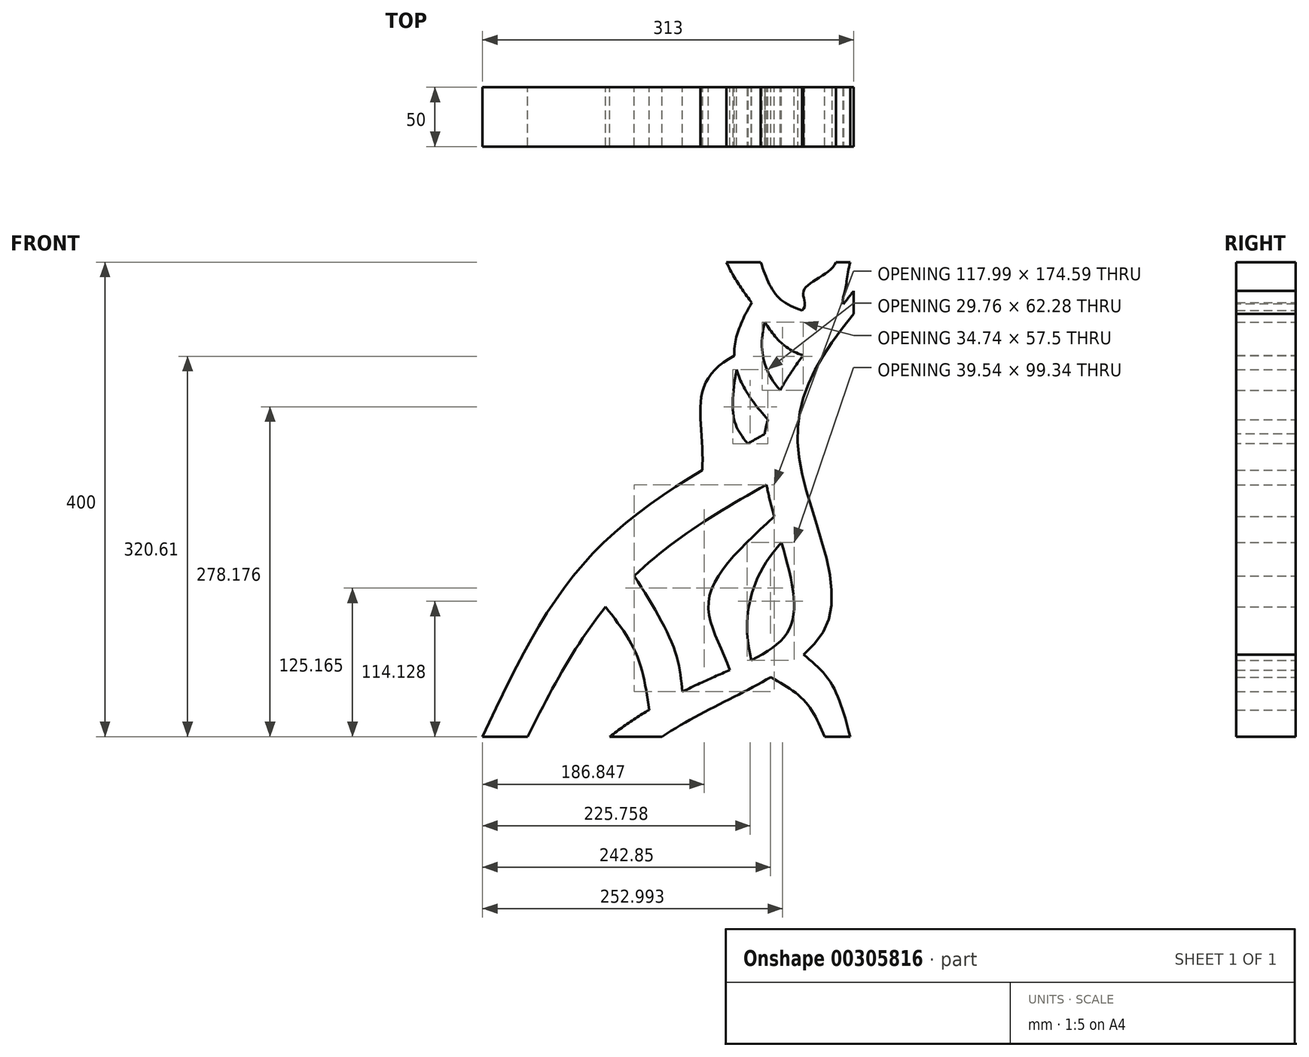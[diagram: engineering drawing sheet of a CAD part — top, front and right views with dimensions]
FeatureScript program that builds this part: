
annotation { "Feature Type Name" : "Feature", "Feature Type Description" : "" }
export const myFeature = defineFeature(function(context is Context, id is Id, definition is map)
    precondition{}
    {
        {
            var Q0;
            Q0=qCreatedBy(makeId("Front.planeOp"),FACE);
            var sketch = newSketch(context, id + "F0", { "sketchPlane" : qUnion([Q0])});
            skLineSegment(sketch, "E0.bottom", {"start": v(161.57, 207.7) * mm, "end": v(-151.43, 207.7) * mm});
            skLineSegment(sketch, "E0.top", {"start": v(161.57, -192.3) * mm, "end": v(-151.43, -192.3) * mm});
            skLineSegment(sketch, "E0.left", {"start": v(161.57, 207.7) * mm, "end": v(161.57, -192.3) * mm});
            skLineSegment(sketch, "E0.right", {"start": v(-151.43, 207.7) * mm, "end": v(-151.43, -192.3) * mm});
            skFitSpline(sketch, "E1", {"points": [v(161.57, 183.5) * mm, v(85.12, 44.75) * mm, v(109.31, -96.4) * mm, v(-44.12, -192.3) * mm], "startDerivative": vector(-382, -492.17) * mm, "endDerivative": vector(-632.26, -490) * mm});
            skFitSpline(sketch, "E2", {"points": [v(161.57, 164.23) * mm, v(115.12, 45.06) * mm, v(139.33, -96.46) * mm, v(0, -192.3) * mm], "startDerivative": vector(-323.93, -389.82) * mm, "endDerivative": vector(-432.8, -289.86) * mm});
            skFitSpline(sketch, "E3", {"points": [v(87.95, 20.15) * mm, v(-36.08, -69.46) * mm, v(-113.36, -192.3) * mm], "startDerivative": vector(-287.2, -159.14) * mm, "endDerivative": vector(-134.26, -271.05) * mm});
            skFitSpline(sketch, "E4", {"points": [v(86.4, 62.77) * mm, v(-60.96, -40.6) * mm, v(-151.43, -192.3) * mm], "startDerivative": vector(-322.1, -181.09) * mm, "endDerivative": vector(-154.33, -329.73) * mm});
            skFitSpline(sketch, "E5", {"points": [v(91.66, -142.16) * mm, v(120.33, -162.57) * mm, v(137.1, -192.3) * mm], "startDerivative": vector(63.12, -36.39) * mm, "endDerivative": vector(28.09, -64.9) * mm});
            skFitSpline(sketch, "E6", {"points": [v(119.32, -123.08) * mm, v(142.68, -147.67) * mm, v(158.5, -192.3) * mm], "startDerivative": vector(55.7, -46.78) * mm, "endDerivative": vector(23.32, -90.23) * mm});
            skFitSpline(sketch, "E7", {"points": [v(100.65, -28.51) * mm, v(73.78, -78.77) * mm, v(75.03, -127.85) * mm], "startDerivative": vector(-88.91, -98.41) * mm, "endDerivative": vector(24.95, -113.83) * mm});
            skFitSpline(sketch, "E8", {"points": [v(94.41, -6.72) * mm, v(39.45, -75.98) * mm, v(57.07, -136.12) * mm], "startDerivative": vector(-135.48, -128.88) * mm, "endDerivative": vector(50.2, -141.27) * mm});
            skFitSpline(sketch, "E9", {"points": [v(54.23, 207.7) * mm, v(81.23, 165.16) * mm, v(119.4, 129.17) * mm], "startDerivative": vector(44.56, -99.42) * mm, "endDerivative": vector(118.17, -31.75) * mm});
            skFitSpline(sketch, "E10", {"points": [v(83.1, 207.7) * mm, v(99.85, 176.33) * mm, v(142.84, 159.86) * mm], "startDerivative": vector(25.78, -76.02) * mm, "endDerivative": vector(99.84, -29.98) * mm});
            skFitSpline(sketch, "E11", {"points": [v(146.4, 207.7) * mm, v(119.4, 183.78) * mm, v(118, 167.02) * mm], "startDerivative": vector(-16.59, -50.41) * mm, "endDerivative": vector(-40.58, -34) * mm});
            skFitSpline(sketch, "E12", {"points": [v(158.5, 207.7) * mm, v(153.85, 181.92) * mm, v(152.97, 172.55) * mm], "startDerivative": vector(-12.64, -48.27) * mm, "endDerivative": vector(10.98, -30.7) * mm});
            skFitSpline(sketch, "E13", {"points": [v(75.43, 173.52) * mm, v(60.75, 128.85) * mm, v(89.2, 75) * mm], "startDerivative": vector(-54.24, -96.72) * mm, "endDerivative": vector(96.14, -103.87) * mm});
            skFitSpline(sketch, "E14", {"points": [v(86.56, 157.05) * mm, v(84.95, 128.85) * mm, v(99.53, 99.55) * mm], "startDerivative": vector(-16.02, -62.32) * mm, "endDerivative": vector(51.54, -60.1) * mm});
            skFitSpline(sketch, "E15", {"points": [v(62.75, 117) * mm, v(60.75, 74.85) * mm, v(72.13, 54.73) * mm], "startDerivative": vector(-16.42, -83.23) * mm, "endDerivative": vector(39.32, -49.75) * mm});
            skFitSpline(sketch, "E16", {"points": [v(60.75, 128.85) * mm, v(35.6, 103.71) * mm, v(32.47, 71.12) * mm, v(33.78, 32.44) * mm], "startDerivative": vector(-112.87, -59.98) * mm, "endDerivative": vector(-6.89, -98.92) * mm});
            skFitSpline(sketch, "E17", {"points": [v(-47.68, -82.88) * mm, v(-21.54, -123.28) * mm, v(-11.06, -169.71) * mm], "startDerivative": vector(59.74, -77.34) * mm, "endDerivative": vector(13.37, -96.33) * mm});
            skFitSpline(sketch, "E18", {"points": [v(-23.58, -56.72) * mm, v(10.06, -118.02) * mm, v(16.93, -154.44) * mm], "startDerivative": vector(70.14, -111.5) * mm, "endDerivative": vector(7.52, -82.35) * mm});
            skSolve(sketch);
        }
        {
            var Q0;
            {var subQ0=sQuery(id+"F0.wireOp",EDGE,"E3");var subQ3=sQuery(id+"F0.wireOp",EDGE,"E1");var subQ4=makeQuery(id+"F0.imprint","INTERSECT",VERTEX,{"derivedFrom":[subQ3,subQ0]});Q0=makeQuery(id+"F0.imprint","IMPRINT",FACE,{"disambiguationData":[TD([[makeQuery(id+"F0.imprint","IMPRINT",EDGE,{"disambiguationData":[TD([[subQ4,1.0]])],"derivedFrom":subQ3}),-1.0]])]});}
            var Q1;
            {var subQ0=sQuery(id+"F0.wireOp",EDGE,"E17");Q1=makeQuery(id+"F0.imprint","IMPRINT",FACE,{"disambiguationData":[TD([[makeQuery(id+"F0.imprint","IMPRINT",EDGE,{"derivedFrom":subQ0}),1.0]])]});}
            var Q2;
            {var subQ0=sQuery(id+"F0.wireOp",EDGE,"E1");var subQ9=sQuery(id+"F0.wireOp",EDGE,"E0.top");var subQ10=makeQuery(id+"F0.imprint","INTERSECT",VERTEX,{"derivedFrom":[subQ9,subQ0]});Q2=makeQuery(id+"F0.imprint","IMPRINT",FACE,{"disambiguationData":[TD([[makeQuery(id+"F0.imprint","IMPRINT",EDGE,{"disambiguationData":[TD([[subQ10,1.0]])],"derivedFrom":subQ9}),-1.0]])]});}
            var Q3;
            {var subQ0=sQuery(id+"F0.wireOp",EDGE,"E5");Q3=makeQuery(id+"F0.imprint","IMPRINT",FACE,{"disambiguationData":[TD([[makeQuery(id+"F0.imprint","IMPRINT",EDGE,{"derivedFrom":subQ0}),1.0]])]});}
            var Q4;
            {var subQ0=sQuery(id+"F0.wireOp",EDGE,"E7");Q4=makeQuery(id+"F0.imprint","IMPRINT",FACE,{"disambiguationData":[TD([[makeQuery(id+"F0.imprint","IMPRINT",EDGE,{"derivedFrom":subQ0}),-1.0]])]});}
            var Q5;
            {var subQ0=sQuery(id+"F0.wireOp",EDGE,"E15");Q5=makeQuery(id+"F0.imprint","IMPRINT",FACE,{"disambiguationData":[TD([[makeQuery(id+"F0.imprint","IMPRINT",EDGE,{"derivedFrom":subQ0}),-1.0]])]});}
            var Q6;
            {var subQ5=sQuery(id+"F0.wireOp",EDGE,"E14");Q6=makeQuery(id+"F0.imprint","IMPRINT",FACE,{"disambiguationData":[TD([[makeQuery(id+"F0.imprint","IMPRINT",EDGE,{"derivedFrom":subQ5}),-1.0]])]});}
            var Q7;
            {var subQ0=sQuery(id+"F0.wireOp",EDGE,"E9");var subQ1=sQuery(id+"F0.wireOp",EDGE,"E0.bottom");var subQ2=makeQuery(id+"F0.imprint","INTERSECT",VERTEX,{"derivedFrom":[subQ1,subQ0]});Q7=makeQuery(id+"F0.imprint","IMPRINT",FACE,{"disambiguationData":[TD([[makeQuery(id+"F0.imprint","IMPRINT",EDGE,{"disambiguationData":[TD([[subQ2,1.0]])],"derivedFrom":subQ1}),1.0]])]});}
            var Q8;
            {var subQ0=sQuery(id+"F0.wireOp",EDGE,"E11");Q8=makeQuery(id+"F0.imprint","IMPRINT",FACE,{"disambiguationData":[TD([[makeQuery(id+"F0.imprint","IMPRINT",EDGE,{"derivedFrom":subQ0}),1.0]])]});}
            extrude(context, id + "F1", {"entities" : qUnion([Q0, Q1, Q2, Q3, Q4, Q5, Q6, Q7, Q8]), "depth" : 50 * mm});
        }
    });
